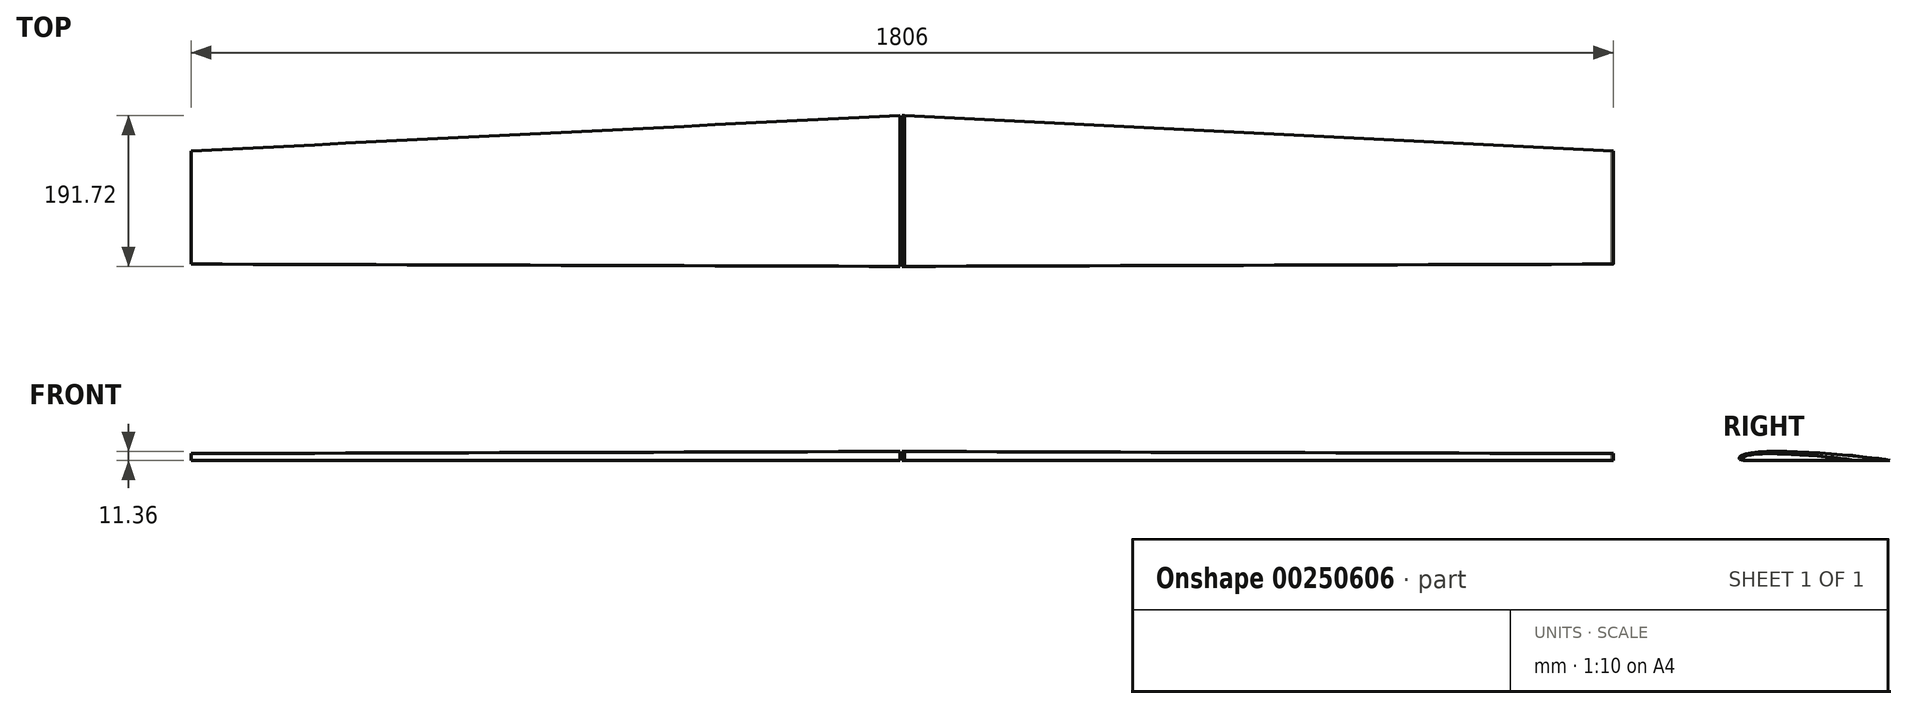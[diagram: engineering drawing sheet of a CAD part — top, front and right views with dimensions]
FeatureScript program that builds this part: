
annotation { "Feature Type Name" : "Feature", "Feature Type Description" : "" }
export const myFeature = defineFeature(function(context is Context, id is Id, definition is map)
    precondition{}
    {
        {
            var Q0;
            Q0=qCreatedBy(makeId("Right.planeOp"),FACE);
            var sketch = newSketch(context, id + "F0", { "sketchPlane" : qUnion([Q0])});
            skLineSegment(sketch, "E0", {"start": v(0, 0) * mm, "end": v(180, 0) * mm});
            skFitSpline(sketch, "E1", {"points": [v(0, 0) * mm, v(-10.97, 1.13) * mm, v(-0.78, 8.46) * mm, v(180, 0) * mm], "startDerivative": vector(-26.9, 0) * mm, "endDerivative": vector(115.45, -21.9) * mm});
            skLineSegment(sketch, "E2.filletArc", {"start": v(0, 0) * mm, "end": v(0, 0) * mm});
            skPoint(sketch, "E3", {"position": v(-4.48, 0) * mm});
            skPoint(sketch, "E4", {"position": v(-2.25, 8.1) * mm});
            skPoint(sketch, "E5", {"position": v(4.32, 9.44) * mm});
            skSolve(sketch);
        }
        {
            var Q0;
            Q0=qSketchRegion(id+"F0",true);
            extrude(context, id + "F1", {"entities" : qUnion([Q0]), "depth" : 3 * mm});
        }
        {
            var Q0;
            Q0=makeQuery(id+"F1.opExtrude","SWEPT_BODY",BODY,{"disambiguationData":[OSD([sQuery(id+"F0.wireOp",EDGE,"E0"),sQuery(id+"F0.wireOp",EDGE,"E1"),sQuery(id+"F0.wireOp",EDGE,"E2.filletArc")])]});
            var Q1;
            Q1=qCreatedBy(makeId("Right.planeOp"),FACE);
            transform(context, id + "F2", {"entities" : qUnion([Q0]), "transformType" : TransformType.TRANSLATION_DISTANCE, "transformDirection" : qUnion([Q1]), "distance" : 900 * mm, "makeCopy" : true});
        }
        {
            var Q0;
            Q0=makeQuery(id+"F2.opPattern","COPY",BODY,{"derivedFrom":makeQuery(id+"F1.opExtrude","SWEPT_BODY",BODY,{"disambiguationData":[OSD([sQuery(id+"F0.wireOp",EDGE,"E0"),sQuery(id+"F0.wireOp",EDGE,"E1"),sQuery(id+"F0.wireOp",EDGE,"E2.filletArc")])]}),"instanceName":"1"});
            var Q1;
            Q1=makeQuery(id+"F2.opPattern","COPY",VERTEX,{"derivedFrom":makeQuery(id+"F1.opExtrude","CAP_VERTEX",VERTEX,{"disambiguationData":[OSD([sQuery(id+"F0.wireOp",EDGE,"E1"),sQuery(id+"F0.wireOp",EDGE,"E2.filletArc")])],"isStart":false}),"instanceName":"1"});
            transform(context, id + "F3", {"entities" : qUnion([Q0]), "transformType" : TransformType.SCALE_UNIFORMLY, "scale" : .75, "scalePoint" : qUnion([Q1]), "makeCopy" : false});
        }
        {
            var Q0;
            Q0=makeQuery(id+"F1.opExtrude","CAP_FACE",FACE,{"disambiguationData":[OSD([sQuery(id+"F0.wireOp",EDGE,"E0"),sQuery(id+"F0.wireOp",EDGE,"E1"),sQuery(id+"F0.wireOp",EDGE,"E2.filletArc")])],"isStart":false});
            var Q1;
            Q1=makeQuery(id+"F2.opPattern","COPY",FACE,{"derivedFrom":makeQuery(id+"F1.opExtrude","CAP_FACE",FACE,{"disambiguationData":[OSD([sQuery(id+"F0.wireOp",EDGE,"E0"),sQuery(id+"F0.wireOp",EDGE,"E1"),sQuery(id+"F0.wireOp",EDGE,"E2.filletArc")])],"isStart":false}),"instanceName":"1"});
            loft(context, id + "F4", {"sheetProfilesArray" : [{ "sheetProfileEntities" : qUnion([Q0]) }, { "sheetProfileEntities" : qUnion([Q1]) }]});
        }
        {
            var Q0;
            Q0=makeQuery(id+"F4.opLoft","SWEPT_BODY",BODY,{"disambiguationData":[OSD([sQuery(id+"F0.wireOp",EDGE,"E0"),sQuery(id+"F0.wireOp",EDGE,"E1")])]});
            var Q1;
            Q1=qCreatedBy(makeId("Right.planeOp"),FACE);
            mirror(context, id + "F5", {"entities" : qUnion([Q0]), "mirrorPlane" : qUnion([Q1])});
        }
    });
